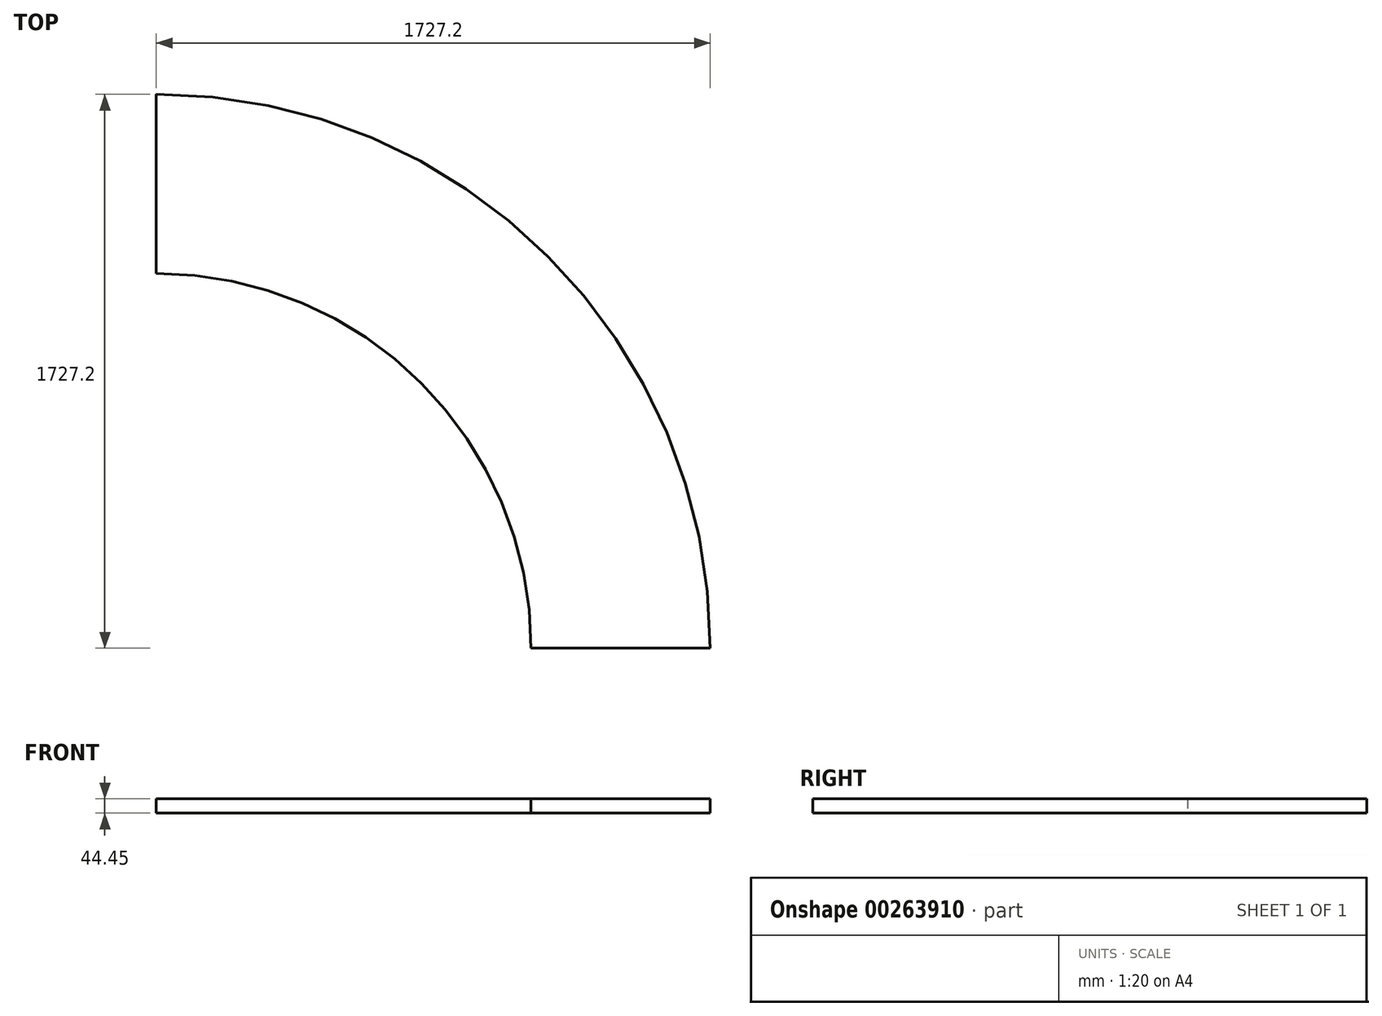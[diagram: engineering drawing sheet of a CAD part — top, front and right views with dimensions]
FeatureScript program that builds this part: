
annotation { "Feature Type Name" : "Feature", "Feature Type Description" : "" }
export const myFeature = defineFeature(function(context is Context, id is Id, definition is map)
    precondition{}
    {
        {
            var Q0;
            Q0=qCreatedBy(makeId("Top.planeOp"),FACE);
            var sketch = newSketch(context, id + "F0", { "sketchPlane" : qUnion([Q0])});
            skArc(sketch, "E0", {"start": v(3657.6, 0) * mm, "mid": v(1828.8, 1828.8) * mm, "end": v(0, 0) * mm});
            skArc(sketch, "E1.0", {"start": v(3556, 0) * mm, "mid": v(1828.8, 1727.2) * mm, "end": v(101.6, 0) * mm});
            skArc(sketch, "E2.0", {"start": v(2997.2, 0) * mm, "mid": v(1828.8, 1168.4) * mm, "end": v(660.4, 0) * mm});
            skLineSegment(sketch, "E3", {"start": v(3556, 0) * mm, "end": v(2997.2, 0) * mm});
            skLineSegment(sketch, "E4", {"start": v(1828.8, 1727.2) * mm, "end": v(1828.8, 1168.4) * mm});
            skSolve(sketch);
        }
        {
            var Q0;
            {var subQ0=sQuery(id+"F0.wireOp",EDGE,"E3");Q0=makeQuery(id+"F0.imprint","IMPRINT",FACE,{"disambiguationData":[TD([[makeQuery(id+"F0.imprint","IMPRINT",EDGE,{"derivedFrom":subQ0}),-1.0]])]});}
            extrude(context, id + "F1", {"entities" : qUnion([Q0]), "depth" : 44.45 * mm});
        }
    });
